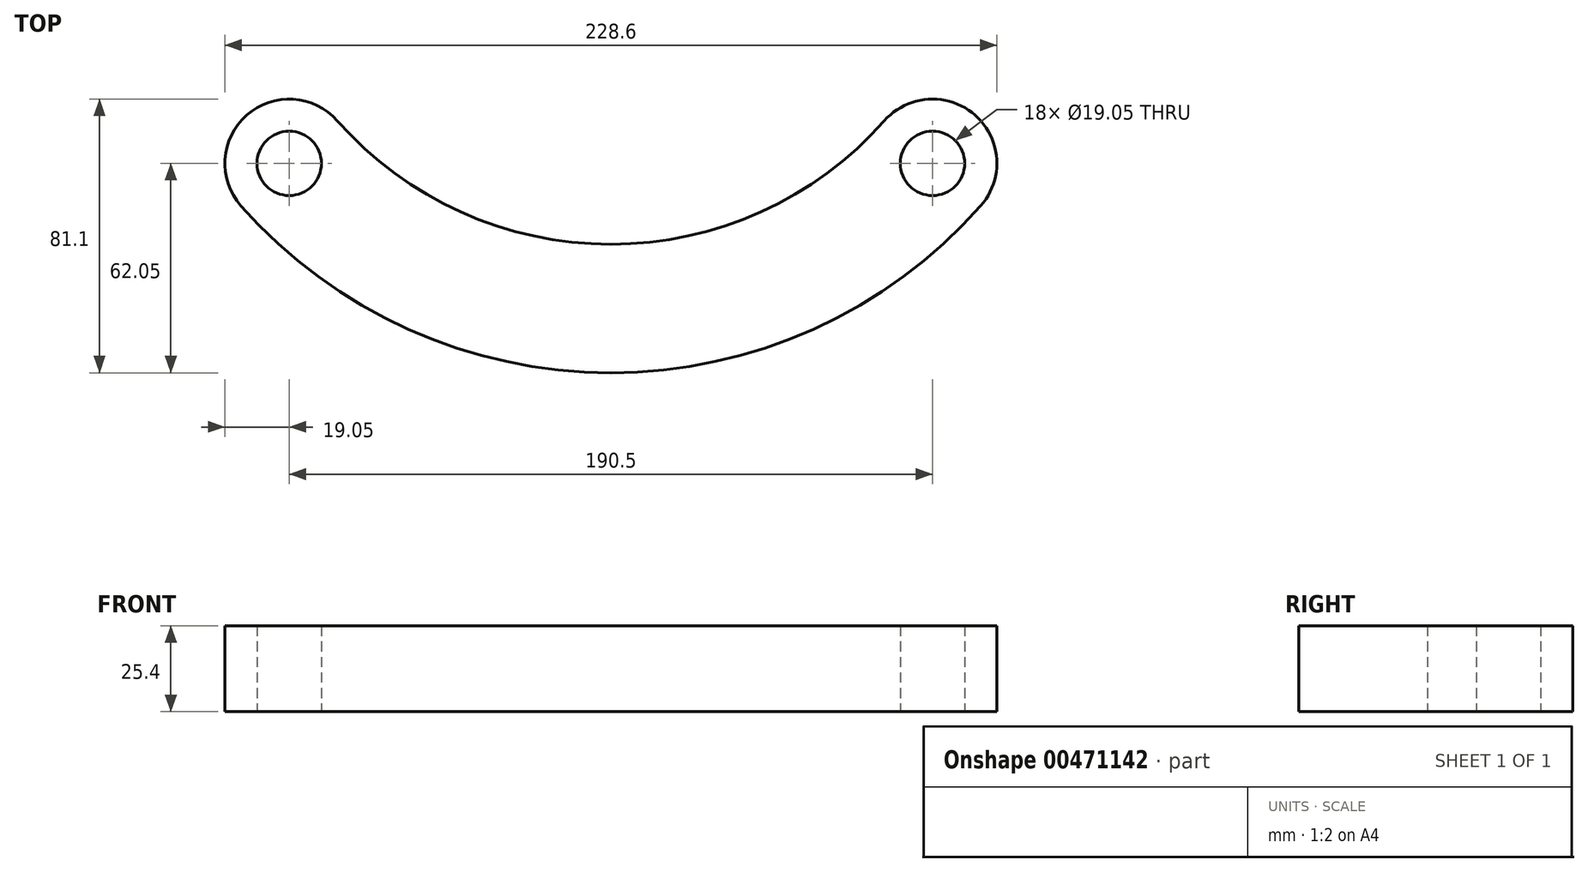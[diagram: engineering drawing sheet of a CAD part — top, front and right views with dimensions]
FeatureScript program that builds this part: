
annotation { "Feature Type Name" : "Feature", "Feature Type Description" : "" }
export const myFeature = defineFeature(function(context is Context, id is Id, definition is map)
    precondition{}
    {
        {
            var Q0;
            Q0=qCreatedBy(makeId("Top.planeOp"),FACE);
            var sketch = newSketch(context, id + "F0", { "sketchPlane" : qUnion([Q0])});
            skCircle(sketch, "E0", {"center": v(0, 0) * mm, "radius": 9.53 * mm});
            skLineSegment(sketch, "E1", {"start": v(0, 0) * mm, "end": v(190.5, 0) * mm, "construction": true});
            skCircle(sketch, "E2", {"center": v(190.5, 0) * mm, "radius": 9.53 * mm});
            skLineSegment(sketch, "E3", {"start": v(0, 0) * mm, "end": v(95.25, 84) * mm, "construction": true});
            skArc(sketch, "E4", {"start": v(14.29, 12.6) * mm, "mid": v(95.25, -23.95) * mm, "end": v(176.21, 12.6) * mm});
            skArc(sketch, "E5", {"start": v(-14.29, -12.6) * mm, "mid": v(95.25, -62.05) * mm, "end": v(204.79, -12.6) * mm});
            skArc(sketch, "E6", {"start": v(176.21, 12.6) * mm, "mid": v(203.1, 14.29) * mm, "end": v(204.79, -12.6) * mm});
            skArc(sketch, "E7", {"start": v(14.29, 12.6) * mm, "mid": v(-12.6, 14.29) * mm, "end": v(-14.29, -12.6) * mm});
            skArc(sketch, "E8", {"start": v(0, 0) * mm, "mid": v(95.25, -43) * mm, "end": v(190.5, 0) * mm, "construction": true});
            skLineSegment(sketch, "E9", {"start": v(95.25, 84) * mm, "end": v(190.5, 0) * mm, "construction": true});
            skSolve(sketch);
        }
        {
            var Q0;
            Q0=makeQuery(id+"F0.imprint","IMPRINT",FACE,{"disambiguationData":[TD([[makeQuery(id+"F0.imprint","IMPRINT",EDGE,{"derivedFrom":sQuery(id+"F0.wireOp",EDGE,"E0")}),-1.0]])]});
            extrude(context, id + "F1", {"entities" : qUnion([Q0]), "depth" : 25.4 * mm});
        }
    });
